# Revit family: rinnai_linear1500_ds
name_source: partatom
category: Specialty Equipment
units: mm (PartAtom-declared; Revit-internal decimal feet)

## family parameters
Always vertical = Yes
Cut with Voids When Loaded = Yes
Host = Wall
Part Type = Normal
Room Calculation Point = No
Round Connector Dimension = Use Diameter
Shared = No

## types (1)
- rinnai_linear1500_ds
    Description = Linear 1500 Double sided Fireplace
    Double Sided = Yes
    Fire Window Wall Cut = 5 mm  [stored 0.0164042 ft]
    Front Offset to middle to middle of fire = 212 mm  [stored 0.695538 ft]
    Manufacturer = Rinnai NZ Ltd
    Model = Linear 1500 Double Sided
    Type Comments = Linear 1500 Double Sided
    URL = www.rinnai.co.nz
    _fire_centre_depth = 212.5 mm  [stored 0.697178 ft]
    _fire_clearceiling = 1000 mm  [stored 3.28084 ft]
    _fire_cleardepth = 1000 mm  [stored 3.28084 ft]
    _fire_clearheight = 400 mm  [stored 1.31234 ft]
    _fire_side_clearance = 400 mm  [stored 1.31234 ft]
    _fire_top = 744 mm  [stored 2.44094 ft]
    _fire_width = 1850 mm  [stored 6.06955 ft]
    _fire_window_top = 311 mm  [stored 1.02034 ft]
    _fire_window_width = 1530 mm  [stored 5.01969 ft]
    _opening_depth = 425 mm  [stored 1.39436 ft]
    _opening_height = 794 mm  [stored 2.60499 ft]
    _opening_width = 1950 mm  [stored 6.39764 ft]
    clearance = 50 mm  [stored 0.164042 ft]
    m_body = Rinnai Body
    m_cowl = Rinnai Cowl
    m_firebox = Rinnai_firebox
    m_flames = Rinnai Flames
    m_flue = Rinnai Flue
    m_frame = Rinnai Black Frame
    m_gas = Rinnai Gas
    m_glass = Rinnai_fireglass
    m_plinth = <By Category>
    m_rinnai = Rinnai_logo
    opening floor offset = 0 mm  [stored 0 ft]
    v_back = No
    v_fireplace = Yes

note: [stored X ft] marks values corroborated as IEEE doubles in the binary element streams (Revit-internal decimal feet)

## geometry (parser evidence)
native form markers: Sweep x48
no freeform markers — native parametric forms only
